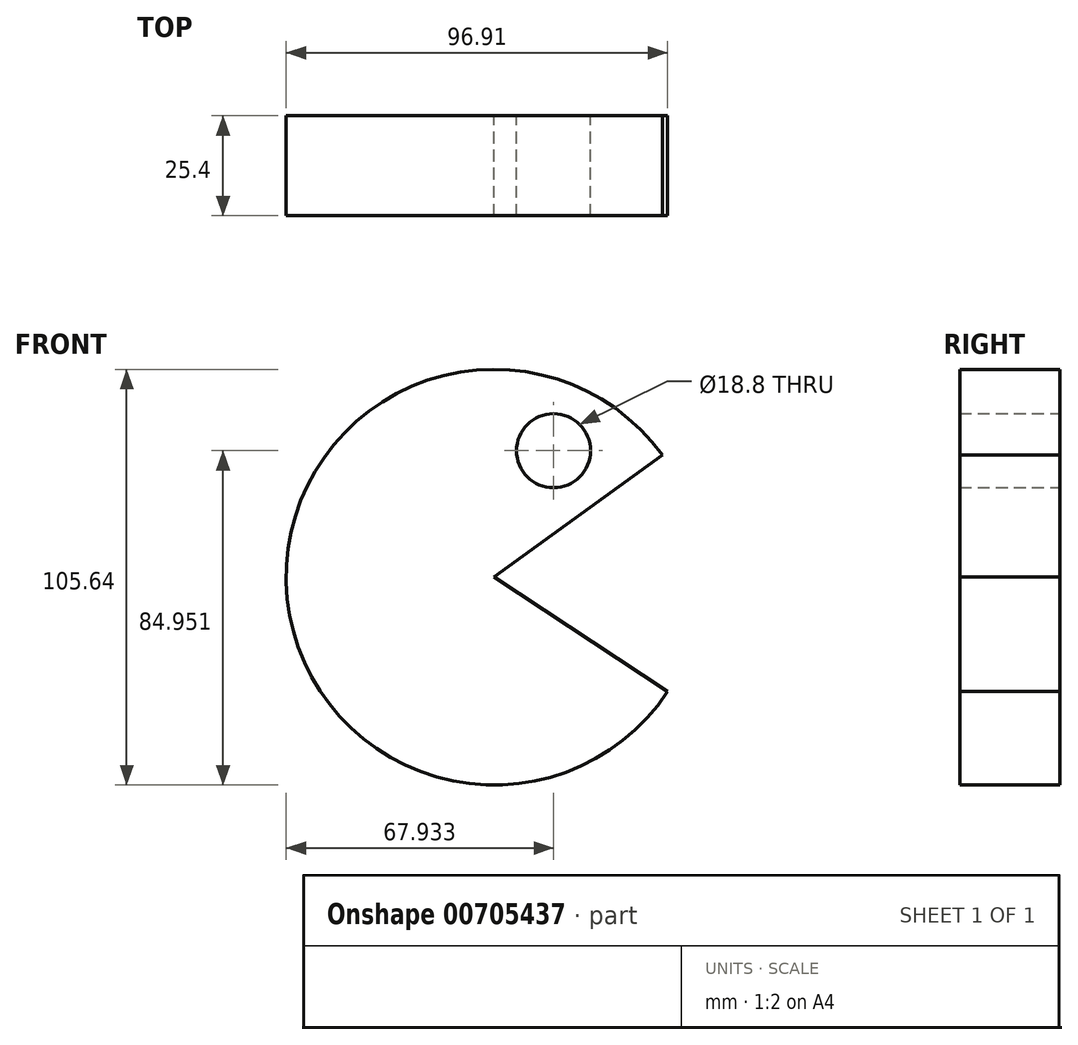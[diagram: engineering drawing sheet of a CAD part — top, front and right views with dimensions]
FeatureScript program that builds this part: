
annotation { "Feature Type Name" : "Feature", "Feature Type Description" : "" }
export const myFeature = defineFeature(function(context is Context, id is Id, definition is map)
    precondition{}
    {
        {
            var Q0;
            Q0=qCreatedBy(makeId("Front.planeOp"),FACE);
            var sketch = newSketch(context, id + "F0", { "sketchPlane" : qUnion([Q0])});
            skArc(sketch, "E0", {"start": v(42.75, 31.02) * mm, "mid": v(-52.8, -1.18) * mm, "end": v(44.1, -29.08) * mm});
            skLineSegment(sketch, "E1", {"start": v(0, 0) * mm, "end": v(42.75, 31.02) * mm});
            skLineSegment(sketch, "E2", {"start": v(0, 0) * mm, "end": v(44.1, -29.08) * mm});
            skCircle(sketch, "E3", {"center": v(15.11, 32.13) * mm, "radius": 9.4 * mm});
            skSolve(sketch);
        }
        {
            var Q0;
            Q0 = qSketchRegion(id + "F0", true);
            extrude(context, id + "F1", {"entities" : qUnion([Q0]), "depth" : 25.4 * mm, "offsetDistance" : 25.4 * mm});
        }
    });
